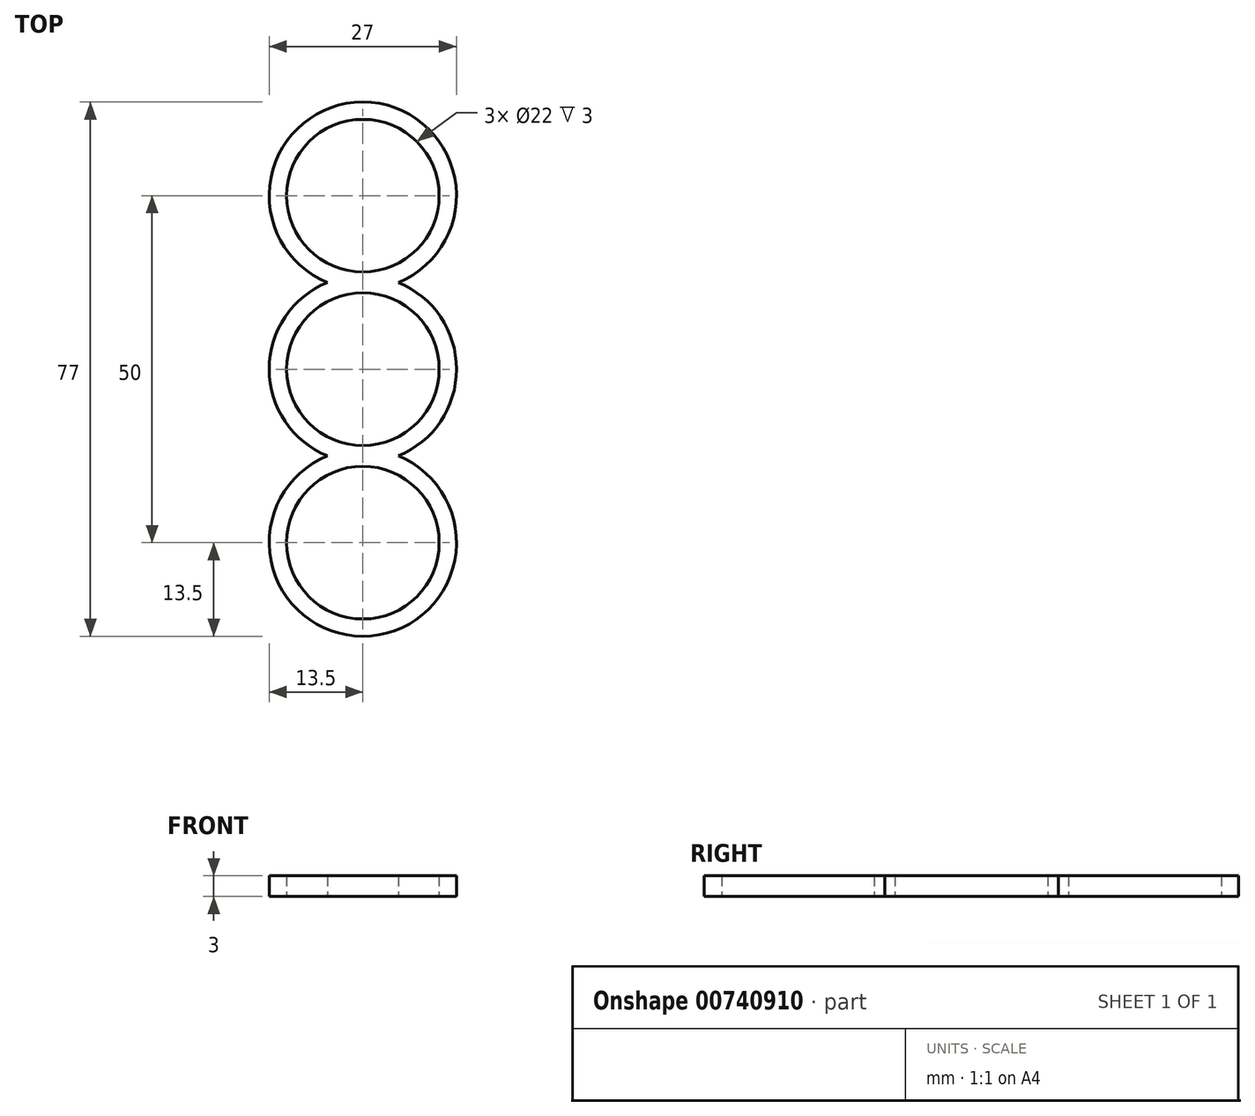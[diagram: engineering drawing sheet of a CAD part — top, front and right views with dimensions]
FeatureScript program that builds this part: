
annotation { "Feature Type Name" : "Feature", "Feature Type Description" : "" }
export const myFeature = defineFeature(function(context is Context, id is Id, definition is map)
    precondition{}
    {
        {
            var Q0;
            Q0=qCreatedBy(makeId("Top.planeOp"),FACE);
            var sketch = newSketch(context, id + "F0", { "sketchPlane" : qUnion([Q0])});
            skArc(sketch, "E0", {"start": v(11, 0) * mm, "mid": v(0, 11) * mm, "end": v(-11, 0) * mm});
            skCircle(sketch, "E1", {"center": v(0, 25) * mm, "radius": 11 * mm});
            skArc(sketch, "E2", {"start": v(5.1, 12.5) * mm, "mid": v(0, 38.5) * mm, "end": v(-5.1, 12.5) * mm});
            skArc(sketch, "E3", {"start": v(-5.1, 12.5) * mm, "mid": v(-11.2, 7.53) * mm, "end": v(-13.5, 0) * mm});
            skLineSegment(sketch, "E4", {"start": v(32.87, 0) * mm, "end": v(-38.42, 0) * mm});
            skArc(sketch, "E5.trimOffspring", {"start": v(13.5, 0) * mm, "mid": v(11.2, 7.53) * mm, "end": v(5.1, 12.5) * mm});
            skArc(sketch, "E6.1.0", {"start": v(5.1, -12.5) * mm, "mid": v(11.2, -7.53) * mm, "end": v(13.5, 0) * mm});
            skArc(sketch, "E6.1.1", {"start": v(-13.5, 0) * mm, "mid": v(-11.2, -7.53) * mm, "end": v(-5.1, -12.5) * mm});
            skArc(sketch, "E6.1.2", {"start": v(-5.1, -12.5) * mm, "mid": v(0, -38.5) * mm, "end": v(5.1, -12.5) * mm});
            skArc(sketch, "E6.1.3", {"start": v(-11, 0) * mm, "mid": v(0, -11) * mm, "end": v(11, 0) * mm});
            skCircle(sketch, "E6.1.4", {"center": v(0, -25) * mm, "radius": 11 * mm});
            skSolve(sketch);
        }
        {
            var Q0;
            Q0 = qSketchRegion(id + "F0", true);
            extrude(context, id + "F1", {"entities" : qUnion([Q0]), "depth" : 3 * mm, "offsetDistance" : 25 * mm});
        }
    });
